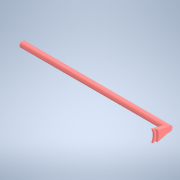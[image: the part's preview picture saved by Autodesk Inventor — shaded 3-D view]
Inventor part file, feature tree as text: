
AUTODESK INVENTOR PART (.ipt)
format: ipt  version: 2022 (Build 260153000, 153)  size: 174,080 bytes
history: native  units: mm
features: extrude x3, sketch x3, other x2, projected_geometry x1
ambient origin geometry x8: Origin, YZ Plane, XZ Plane, XY Plane, X Axis, Y Axis, Z Axis, Center Point
bodies: Body1 (feature_tree)
feature tree (9):
  other  "Твердое тело1"
  extrude  "Выдавливание1"  Depth=1.8mm TaperAngle=0.0deg
  extrude  "Выдавливание2"  Depth=1.0mm TaperAngle=0.0deg
  extrude  "Выдавливание3"  Depth=128.0mm TaperAngle=0.0deg
  sketch  "Эскиз1"
  sketch  "Эскиз3"
  projected_geometry  "Спроецированная петля3"
  sketch  "Эскиз4"
  other  "Reliz"
